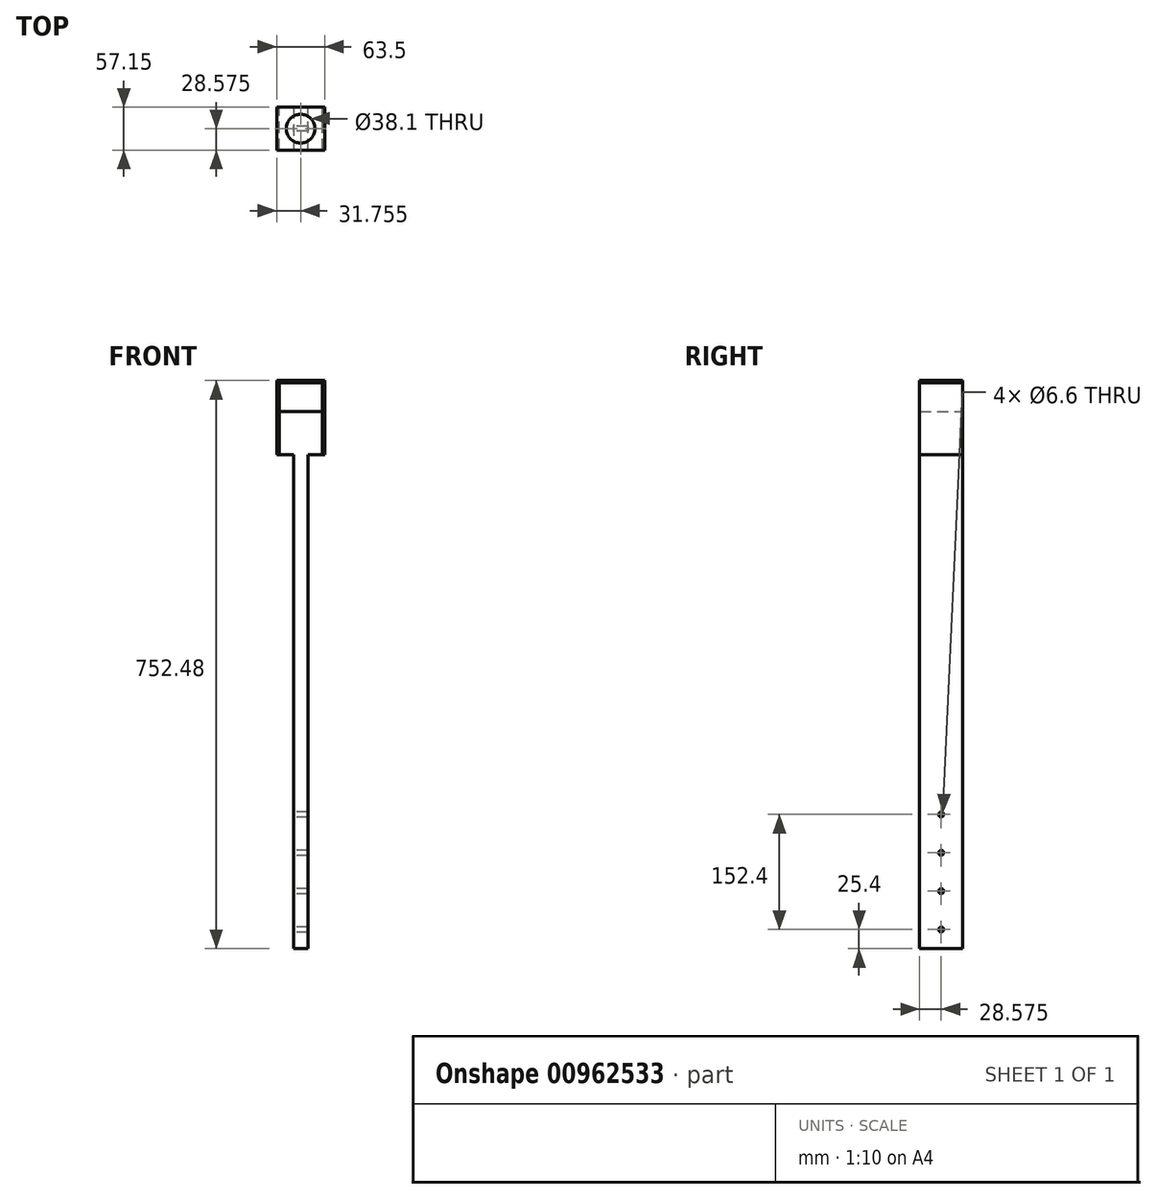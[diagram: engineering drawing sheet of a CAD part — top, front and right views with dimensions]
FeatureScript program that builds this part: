
annotation { "Feature Type Name" : "Feature", "Feature Type Description" : "" }
export const myFeature = defineFeature(function(context is Context, id is Id, definition is map)
    precondition{}
    {
        {
            var Q0;
            Q0=qCreatedBy(makeId("Top.planeOp"),FACE);
            var sketch = newSketch(context, id + "F0", { "sketchPlane" : qUnion([Q0])});
            skLineSegment(sketch, "E0.bottom", {"start": v(0, 0) * mm, "end": v(19.05, 0) * mm});
            skLineSegment(sketch, "E0.top", {"start": v(0, 57.15) * mm, "end": v(19.05, 57.15) * mm});
            skLineSegment(sketch, "E0.left", {"start": v(0, 0) * mm, "end": v(0, 57.15) * mm});
            skLineSegment(sketch, "E0.right", {"start": v(19.05, 0) * mm, "end": v(19.05, 57.15) * mm});
            skSolve(sketch);
        }
        {
            var Q0;
            Q0=makeQuery(id+"F0.imprint","IMPRINT",FACE,{"disambiguationData":[TD([[makeQuery(id+"F0.imprint","IMPRINT",EDGE,{"derivedFrom":sQuery(id+"F0.wireOp",EDGE,"E0.bottom")}),1.0]])]});
            extrude(context, id + "F1", {"entities" : qUnion([Q0]), "depth" : 711.2 * mm, "offsetDistance" : 25.4 * mm});
        }
        {
            var Q0;
            Q0=makeQuery(id+"F1.opExtrude","SWEPT_FACE",FACE,{"disambiguationData":[OSD([sQuery(id+"F0.wireOp",EDGE,"E0.left")])]});
            var sketch = newSketch(context, id + "F2", { "sketchPlane" : qUnion([Q0])});
            skLineSegment(sketch, "E1.bottom", {"start": v(-57.15, 711.2) * mm, "end": v(0, 711.2) * mm});
            skLineSegment(sketch, "E1.top", {"start": v(-57.15, 654.05) * mm, "end": v(0, 654.05) * mm});
            skLineSegment(sketch, "E1.left", {"start": v(-57.15, 711.2) * mm, "end": v(-57.15, 654.05) * mm});
            skLineSegment(sketch, "E1.right", {"start": v(0, 711.2) * mm, "end": v(0, 654.05) * mm});
            skSolve(sketch);
        }
        {
            var Q0;
            Q0=makeQuery(id+"F2.imprint","IMPRINT",FACE,{"disambiguationData":[TD([[makeQuery(id+"F2.imprint","IMPRINT",EDGE,{"derivedFrom":sQuery(id+"F2.wireOp",EDGE,"E1.bottom")}),1.0]])]});
            extrude(context, id + "F3", {"entities" : qUnion([Q0]), "operationType" : NewBodyOperationType.ADD, "depth" : 19.05 * mm, "offsetDistance" : 25.4 * mm});
        }
        {
            var Q0;
            Q0=makeQuery(id+"F1.opExtrude","SWEPT_FACE",FACE,{"disambiguationData":[OSD([sQuery(id+"F0.wireOp",EDGE,"E0.right")])]});
            var sketch = newSketch(context, id + "F4", { "sketchPlane" : qUnion([Q0])});
            skLineSegment(sketch, "E2.bottom", {"start": v(0, 711.2) * mm, "end": v(57.15, 711.2) * mm});
            skLineSegment(sketch, "E2.top", {"start": v(0, 654.05) * mm, "end": v(57.15, 654.05) * mm});
            skLineSegment(sketch, "E2.left", {"start": v(0, 711.2) * mm, "end": v(0, 654.05) * mm});
            skLineSegment(sketch, "E2.right", {"start": v(57.15, 711.2) * mm, "end": v(57.15, 654.05) * mm});
            skSolve(sketch);
        }
        {
            var Q0;
            Q0=makeQuery(id+"F4.imprint","IMPRINT",FACE,{"disambiguationData":[TD([[makeQuery(id+"F4.imprint","IMPRINT",EDGE,{"derivedFrom":sQuery(id+"F4.wireOp",EDGE,"E2.bottom")}),-1.0]])]});
            extrude(context, id + "F5", {"entities" : qUnion([Q0]), "operationType" : NewBodyOperationType.ADD, "depth" : 19.05 * mm, "offsetDistance" : 25.4 * mm});
        }
        {
            var Q0;
            Q0=makeQuery(id+"F5.boolean.opBoolean","MERGE",FACE,{"derivedFrom":[makeQuery(id+"F3.boolean.opBoolean","MERGE",FACE,{"derivedFrom":[makeQuery(id+"F1.opExtrude","CAP_FACE",FACE,{"disambiguationData":[OSD([sQuery(id+"F0.wireOp",EDGE,"E0.bottom"),sQuery(id+"F0.wireOp",EDGE,"E0.top"),sQuery(id+"F0.wireOp",EDGE,"E0.left"),sQuery(id+"F0.wireOp",EDGE,"E0.right")])],"isStart":false}),makeQuery(id+"F3.opExtrude","SWEPT_FACE",FACE,{"disambiguationData":[OSD([sQuery(id+"F2.wireOp",EDGE,"E1.bottom")])]})]}),makeQuery(id+"F5.opExtrude","SWEPT_FACE",FACE,{"disambiguationData":[OSD([sQuery(id+"F4.wireOp",EDGE,"E2.bottom")])]})]});
            cPlane(context, id + "F6", {"entities" : qUnion([Q0]), "cplaneType" : CPlaneType.OFFSET, "offset" : 38.1 * mm, "width" : 152.4 * mm, "height" : 152.4 * mm});
        }
        {
            var Q0;
            Q0=qCreatedBy(id+"F6.planeOp",FACE);
            var sketch = newSketch(context, id + "F7", { "sketchPlane" : qUnion([Q0])});
            skLineSegment(sketch, "E3.0", {"start": v(38.1, 0) * mm, "end": v(38.1, 57.15) * mm});
            skLineSegment(sketch, "E4.0", {"start": v(-19.05, 0) * mm, "end": v(-19.05, 57.15) * mm});
            skLineSegment(sketch, "E5.bottom", {"start": v(-22.23, 57.15) * mm, "end": v(41.27, 57.15) * mm});
            skLineSegment(sketch, "E5.top", {"start": v(-22.22, 0) * mm, "end": v(41.28, 0) * mm});
            skLineSegment(sketch, "E5.left", {"start": v(-22.23, 57.15) * mm, "end": v(-22.22, 0) * mm});
            skLineSegment(sketch, "E5.right", {"start": v(41.27, 57.15) * mm, "end": v(41.28, 0) * mm});
            skSolve(sketch);
        }
        {
            var Q0;
            Q0 = qSketchRegion(id + "F7", true);
            extrude(context, id + "F8", {"entities" : qUnion([Q0]), "depth" : 3.17 * mm, "offsetDistance" : 25.4 * mm});
        }
        {
            var Q0;
            Q0=makeQuery(id+"F8.opExtrude","CAP_FACE",FACE,{"disambiguationData":[OSD([sQuery(id+"F7.wireOp",EDGE,"E5.bottom"),sQuery(id+"F7.wireOp",EDGE,"E5.top"),sQuery(id+"F7.wireOp",EDGE,"E5.left"),sQuery(id+"F7.wireOp",EDGE,"E5.right")])],"isStart":true});
            var sketch = newSketch(context, id + "F9", { "sketchPlane" : qUnion([Q0])});
            skLineSegment(sketch, "E6.bottom", {"start": v(-22.23, -57.15) * mm, "end": v(-19.05, -57.15) * mm});
            skLineSegment(sketch, "E6.top", {"start": v(-22.23, 0) * mm, "end": v(-19.05, 0) * mm});
            skLineSegment(sketch, "E6.left", {"start": v(-22.23, -57.15) * mm, "end": v(-22.23, 0) * mm});
            skLineSegment(sketch, "E6.right", {"start": v(-19.05, -57.15) * mm, "end": v(-19.05, 0) * mm});
            skLineSegment(sketch, "E7.bottom", {"start": v(41.27, -57.15) * mm, "end": v(38.1, -57.15) * mm});
            skLineSegment(sketch, "E7.top", {"start": v(41.27, 0) * mm, "end": v(38.1, 0) * mm});
            skLineSegment(sketch, "E7.left", {"start": v(41.27, -57.15) * mm, "end": v(41.27, 0) * mm});
            skLineSegment(sketch, "E7.right", {"start": v(38.1, -57.15) * mm, "end": v(38.1, 0) * mm});
            skSolve(sketch);
        }
        {
            var Q0;
            Q0 = qSketchRegion(id + "F9", true);
            var Q1;
            Q1=makeQuery(id+"F5.opExtrude","SWEPT_FACE",FACE,{"disambiguationData":[OSD([sQuery(id+"F4.wireOp",EDGE,"E2.top")])]});
            extrude(context, id + "F10", {"entities" : qUnion([Q0]), "endBound" : BoundingType.UP_TO_SURFACE, "depth" : 25.4 * mm, "endBoundEntityFace" : qUnion([Q1]), "offsetDistance" : 25.4 * mm});
        }
        {
            var Q0;
            Q0=makeQuery(id+"F8.opExtrude","CAP_FACE",FACE,{"disambiguationData":[OSD([sQuery(id+"F7.wireOp",EDGE,"E5.bottom"),sQuery(id+"F7.wireOp",EDGE,"E5.top"),sQuery(id+"F7.wireOp",EDGE,"E5.left"),sQuery(id+"F7.wireOp",EDGE,"E5.right")])],"isStart":false});
            var sketch = newSketch(context, id + "F11", { "sketchPlane" : qUnion([Q0])});
            skPoint(sketch, "E8", {"position": v(9.52, 57.15) * mm});
            skPoint(sketch, "E9", {"position": v(-22.23, 28.57) * mm});
            skLineSegment(sketch, "E10", {"start": v(-22.23, 28.57) * mm, "end": v(41.27, 28.57) * mm, "construction": true});
            skLineSegment(sketch, "E11", {"start": v(9.52, 57.15) * mm, "end": v(9.53, 0) * mm, "construction": true});
            skCircle(sketch, "E12", {"center": v(9.52, 28.57) * mm, "radius": 19.05 * mm});
            skSolve(sketch);
        }
        {
            var Q0;
            Q0=makeQuery(id+"F11.imprint","IMPRINT",FACE,{"disambiguationData":[TD([[makeQuery(id+"F11.imprint","IMPRINT",EDGE,{"derivedFrom":sQuery(id+"F11.wireOp",EDGE,"E12")}),1.0]])]});
            extrude(context, id + "F12", {"entities" : qUnion([Q0]), "operationType" : NewBodyOperationType.REMOVE, "endBound" : BoundingType.UP_TO_NEXT, "oppositeDirection" : true, "depth" : 25.4 * mm, "offsetDistance" : 25.4 * mm});
        }
        {
            var Q0;
            Q0=makeQuery(id+"F1.opExtrude","SWEPT_FACE",FACE,{"disambiguationData":[OSD([sQuery(id+"F0.wireOp",EDGE,"E0.left")])]});
            var sketch = newSketch(context, id + "F13", { "sketchPlane" : qUnion([Q0])});
            skLineSegment(sketch, "E13", {"start": v(-28.57, 0) * mm, "end": v(-28.57, 752.48) * mm, "construction": true});
            skCircle(sketch, "E14", {"center": v(-28.58, 25.4) * mm, "radius": 3.3 * mm});
            skCircle(sketch, "E15", {"center": v(-28.58, 76.2) * mm, "radius": 3.3 * mm});
            skCircle(sketch, "E16", {"center": v(-28.58, 127) * mm, "radius": 3.3 * mm});
            skCircle(sketch, "E17", {"center": v(-28.58, 177.8) * mm, "radius": 3.3 * mm});
            skSolve(sketch);
        }
        {
            var Q0;
            Q0 = qSketchRegion(id + "F13", true);
            extrude(context, id + "F14", {"entities" : qUnion([Q0]), "operationType" : NewBodyOperationType.REMOVE, "endBound" : BoundingType.UP_TO_NEXT, "oppositeDirection" : true, "depth" : 25.4 * mm, "offsetDistance" : 25.4 * mm});
        }
    });
